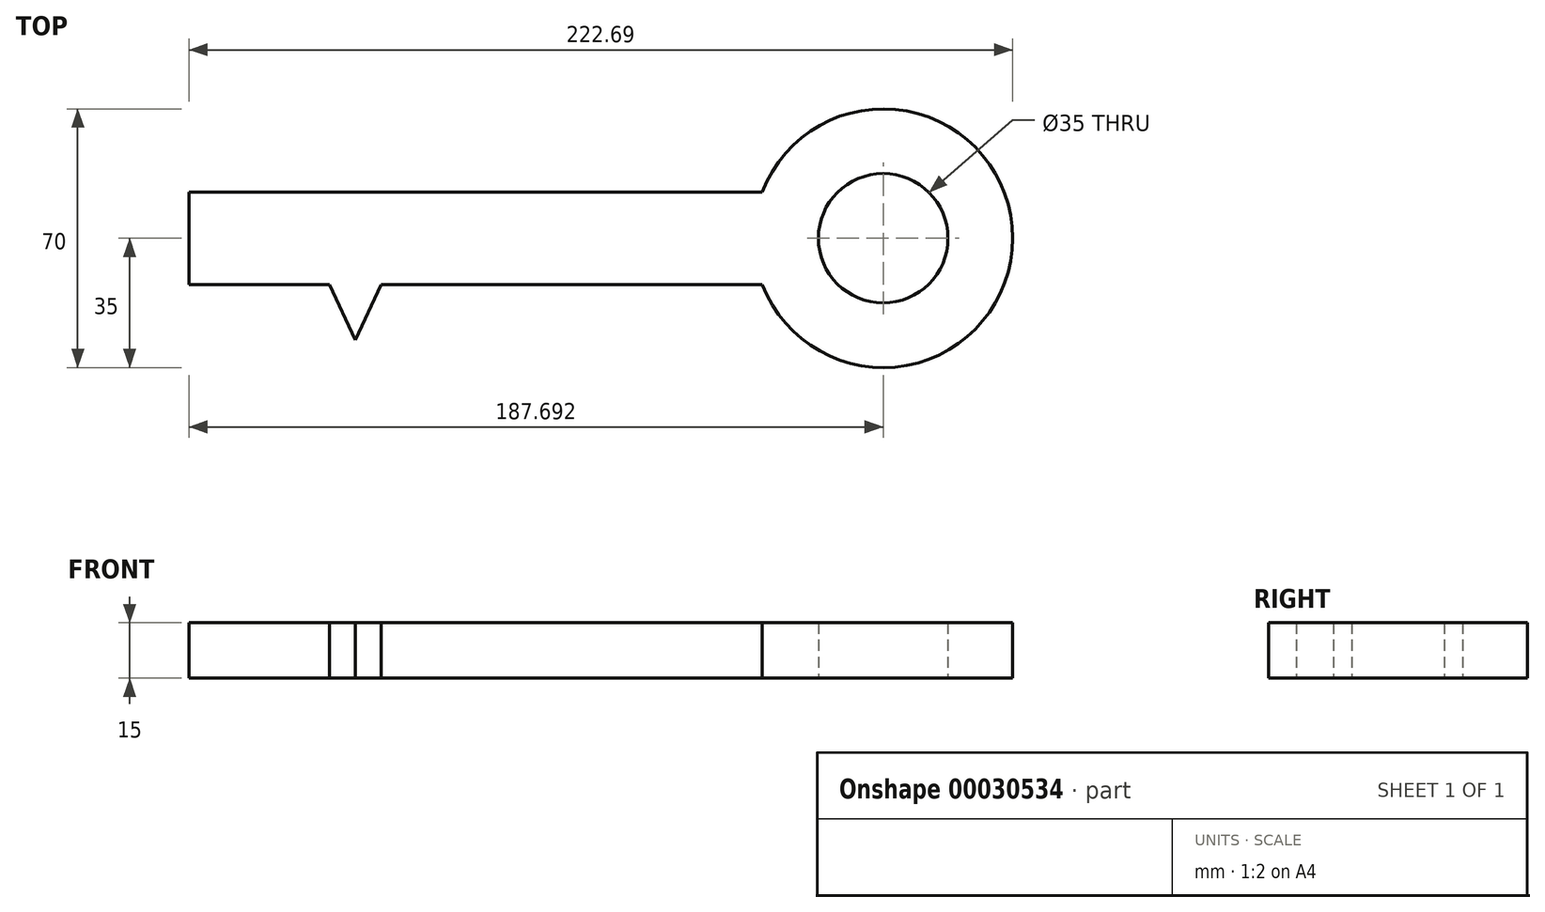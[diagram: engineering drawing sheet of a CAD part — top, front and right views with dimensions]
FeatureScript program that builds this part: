
annotation { "Feature Type Name" : "Feature", "Feature Type Description" : "" }
export const myFeature = defineFeature(function(context is Context, id is Id, definition is map)
    precondition{}
    {
        {
            var Q0;
            Q0=qCreatedBy(makeId("Top.planeOp"),FACE);
            var sketch = newSketch(context, id + "F0", { "sketchPlane" : qUnion([Q0])});
            skLineSegment(sketch, "E0.bottom", {"start": v(-115.75, 25) * mm, "end": v(39.25, 25) * mm});
            skLineSegment(sketch, "E0.top", {"start": v(-115.75, 0) * mm, "end": v(39.25, 0) * mm});
            skLineSegment(sketch, "E0.left", {"start": v(-115.75, 25) * mm, "end": v(-115.75, 0) * mm});
            skLineSegment(sketch, "E1.bottom", {"start": v(-115.75, 0) * mm, "end": v(-105.75, 0) * mm});
            skLineSegment(sketch, "E1.top", {"start": v(-115.75, -30) * mm, "end": v(-105.75, -30) * mm});
            skLineSegment(sketch, "E1.left", {"start": v(-115.75, 0) * mm, "end": v(-115.75, -30) * mm});
            skLineSegment(sketch, "E1.right", {"start": v(-105.75, 0) * mm, "end": v(-105.75, -30) * mm});
            skLineSegment(sketch, "E2.bottom", {"start": v(-95.75, 0) * mm, "end": v(-87.75, 0) * mm});
            skLineSegment(sketch, "E2.top", {"start": v(-95.75, -15) * mm, "end": v(-87.75, -15) * mm});
            skLineSegment(sketch, "E2.left", {"start": v(-95.75, 0) * mm, "end": v(-95.75, -15) * mm});
            skLineSegment(sketch, "E2.right", {"start": v(-87.75, 0) * mm, "end": v(-87.75, -15) * mm});
            skLineSegment(sketch, "E3", {"start": v(-77.75, 0) * mm, "end": v(-70.75, -15) * mm});
            skLineSegment(sketch, "E4", {"start": v(-70.75, -15) * mm, "end": v(-63.75, 0) * mm});
            skArc(sketch, "E5", {"start": v(39.25, 0) * mm, "mid": v(106.94, 12.5) * mm, "end": v(39.25, 25) * mm});
            skCircle(sketch, "E6", {"center": v(71.94, 12.5) * mm, "radius": 17.5 * mm});
            skLineSegment(sketch, "E7", {"start": v(-115.75, 12.5) * mm, "end": v(71.94, 12.5) * mm, "construction": true});
            skSolve(sketch);
        }
        {
            var Q0;
            Q0=makeQuery(id+"F0.imprint","IMPRINT",FACE,{"disambiguationData":[TD([[makeQuery(id+"F0.imprint","IMPRINT",EDGE,{"derivedFrom":sQuery(id+"F0.wireOp",EDGE,"E0.bottom")}),-1.0]])]});
            var Q1;
            {var subQ1=sQuery(id+"F0.wireOp",EDGE,"E3");Q1=makeQuery(id+"F0.imprint","IMPRINT",FACE,{"disambiguationData":[TD([[makeQuery(id+"F0.imprint","IMPRINT",EDGE,{"derivedFrom":subQ1}),1.0]])]});}
            var Q2;
            Q2=makeQuery(id+"F0.imprint","IMPRINT",FACE,{"disambiguationData":[TD([[makeQuery(id+"F0.imprint","IMPRINT",EDGE,{"derivedFrom":sQuery(id+"F0.wireOp",EDGE,"E2.bottom")}),-1.0]])]});
            var Q3;
            Q3=makeQuery(id+"F0.imprint","IMPRINT",FACE,{"disambiguationData":[TD([[makeQuery(id+"F0.imprint","IMPRINT",EDGE,{"derivedFrom":sQuery(id+"F0.wireOp",EDGE,"E1.bottom")}),-1.0]])]});
            extrude(context, id + "F1", {"entities" : qUnion([Q0, Q1, Q2, Q3]), "depth" : 15 * mm});
        }
    });
